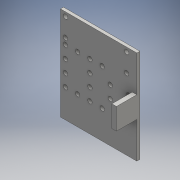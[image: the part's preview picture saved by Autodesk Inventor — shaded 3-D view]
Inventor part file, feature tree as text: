
AUTODESK INVENTOR PART (.ipt)
format: ipt  version: 2016 (Build 200138000, 138)  size: 174,080 bytes
history: native  units: mm
features: sketch x3, extrude x2, hole x1
ambient origin geometry x8: Origin, YZ Plane, XZ Plane, XY Plane, X Axis, Y Axis, Z Axis, Center Point
bodies: Solid1 (feature_tree)
feature tree (6):
  extrude  "Extrusion1"  Depth=92.0mm
  extrude  "Extrusion2"  Depth=18.0mm
  hole  "Hole1"  [1 undecoded]
  sketch  "Sketch1"  dims[d0=75.0mm d1=92.0mm]
  sketch  "Sketch3"  dims[d6=4.35mm d7=18.0mm]
  sketch  "Sketch5"  dims[d8=4.35mm d9=18.0mm d10=4.35mm d11=12.0mm d12=4.35mm d13=4.35mm d14=12.0mm d15=4.35mm d16=4.35mm d17=12.0mm d18=4.35mm d19=12.0mm d20=12.0mm d21=12.0mm d22=3.0mm d23=0.0mm d24=10.5mm d25=4.5mm d26=21.0mm d27=20.0mm d28=0.0mm d29=4.35mm d30=6.0mm d31=8.0mm d32=4.35mm d33=6.0mm d34=4.35mm d35=18.0mm d36=4.35mm d37=4.35mm d38=5.0mm d39=6.0mm d40=4.35mm d41=5.0mm d42=4.35mm d43=24.0mm d44=4.35mm d45=4.35mm d46=4.35mm d47=18.0mm d48=6.0mm d49=6.0mm d50=6.0mm d51=6.0mm d52=6.0mm d53=12.0mm d54=4.35mm d55=60.0mm d56=4.35mm d57=4.35mm d58=6.0mm d59=4.0mm d60=2.0mm d61=90.0deg d62=8.0mm d63=20.594885mm]
note: 1 required parameter value undecoded (feature->parameter linkage not recoverable at this tier; creation-order binding heuristic only, values carry confidence <= 0.55)
